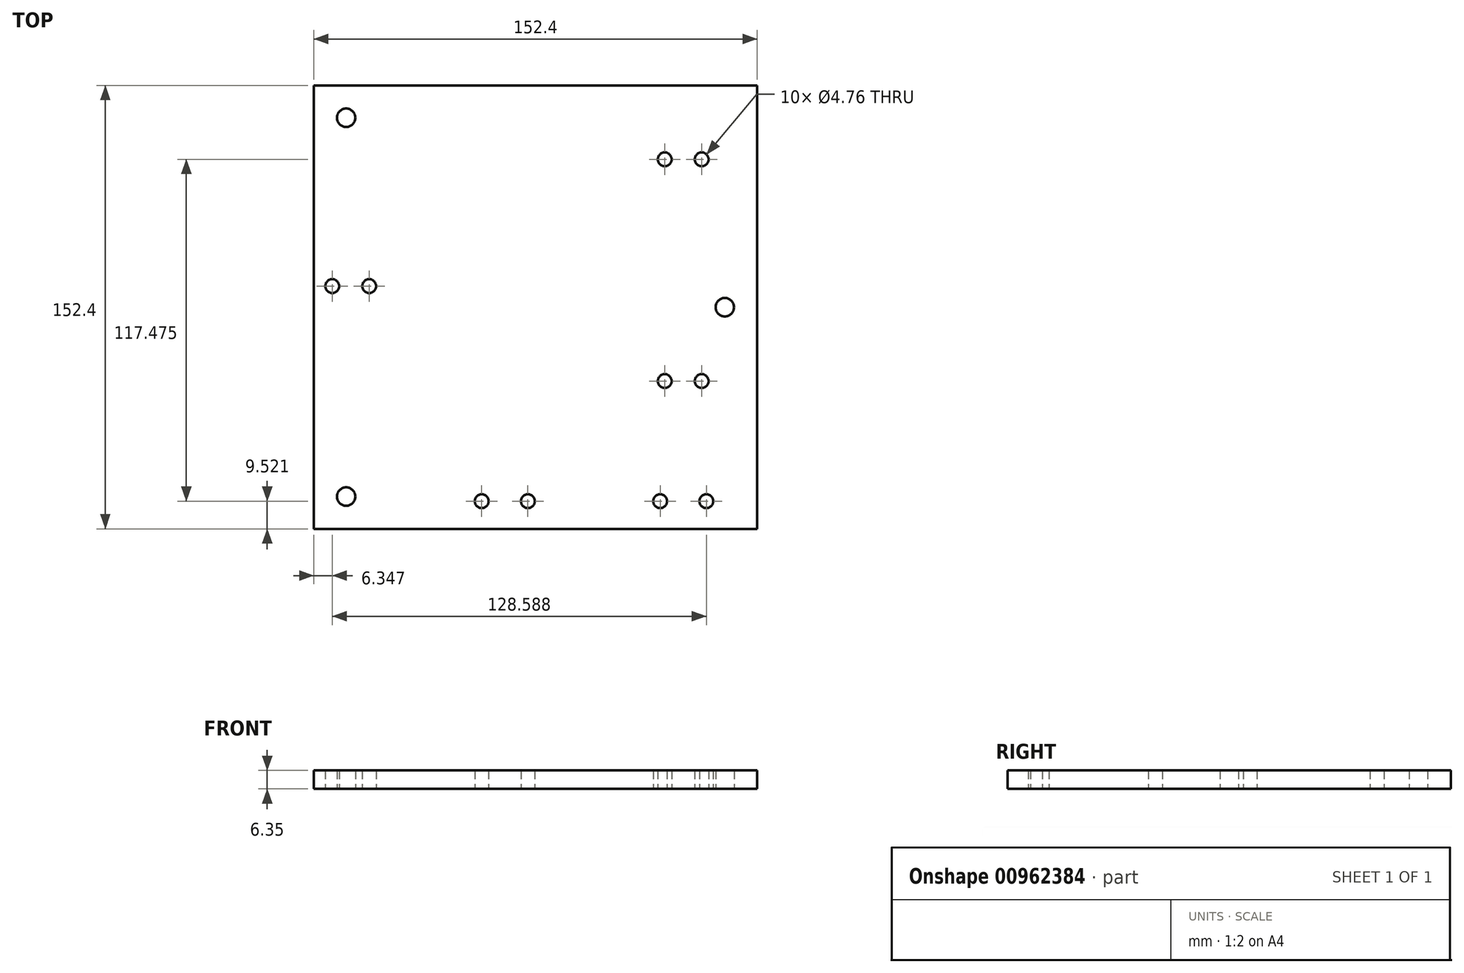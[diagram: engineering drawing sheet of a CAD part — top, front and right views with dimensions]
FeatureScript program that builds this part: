
annotation { "Feature Type Name" : "Feature", "Feature Type Description" : "" }
export const myFeature = defineFeature(function(context is Context, id is Id, definition is map)
    precondition{}
    {
        {
            var Q0;
            Q0=qCreatedBy(makeId("Top.planeOp"),FACE);
            var sketch = newSketch(context, id + "F0", { "sketchPlane" : qUnion([Q0])});
            skLineSegment(sketch, "E0.bottom", {"start": v(-78.32, 75.32) * mm, "end": v(74.08, 75.32) * mm});
            skLineSegment(sketch, "E0.top", {"start": v(-78.32, -77.08) * mm, "end": v(74.08, -77.08) * mm});
            skLineSegment(sketch, "E0.left", {"start": v(-78.32, 75.32) * mm, "end": v(-78.32, -77.08) * mm});
            skLineSegment(sketch, "E0.right", {"start": v(74.08, 75.32) * mm, "end": v(74.08, -77.08) * mm});
            skCircle(sketch, "E1", {"center": v(-67.21, -65.97) * mm, "radius": 3.18 * mm});
            skCircle(sketch, "E2", {"center": v(-67.21, 64.2) * mm, "radius": 3.18 * mm});
            skCircle(sketch, "E3", {"center": v(62.96, -0.88) * mm, "radius": 3.18 * mm});
            skCircle(sketch, "E4", {"center": v(42.33, -26.28) * mm, "radius": 6.35 * mm, "construction": true});
            skCircle(sketch, "E5", {"center": v(42.33, -26.28) * mm, "radius": 2.38 * mm});
            skCircle(sketch, "E6", {"center": v(42.33, 49.92) * mm, "radius": 6.35 * mm, "construction": true});
            skCircle(sketch, "E7", {"center": v(42.33, 49.92) * mm, "radius": 2.38 * mm});
            skCircle(sketch, "E8", {"center": v(-71.97, 6.35) * mm, "radius": 2.38 * mm});
            skCircle(sketch, "E9", {"center": v(-59.27, 6.35) * mm, "radius": 2.38 * mm});
            skLineSegment(sketch, "E10.bottom", {"start": v(-28.54, -77.08) * mm, "end": v(3.21, -77.08) * mm, "construction": true});
            skLineSegment(sketch, "E10.top", {"start": v(-28.54, -58.03) * mm, "end": v(3.21, -58.03) * mm, "construction": true});
            skLineSegment(sketch, "E10.left", {"start": v(-28.54, -77.08) * mm, "end": v(-28.54, -58.03) * mm, "construction": true});
            skLineSegment(sketch, "E10.right", {"start": v(3.21, -77.08) * mm, "end": v(3.21, -58.03) * mm, "construction": true});
            skCircle(sketch, "E11", {"center": v(-20.6, -67.56) * mm, "radius": 2.38 * mm});
            skCircle(sketch, "E12", {"center": v(-4.73, -67.56) * mm, "radius": 2.38 * mm});
            skLineSegment(sketch, "E13.bottom", {"start": v(32.8, -77.08) * mm, "end": v(64.55, -77.08) * mm, "construction": true});
            skLineSegment(sketch, "E13.top", {"start": v(32.8, -58.03) * mm, "end": v(64.55, -58.03) * mm, "construction": true});
            skLineSegment(sketch, "E13.left", {"start": v(32.8, -77.08) * mm, "end": v(32.8, -58.03) * mm, "construction": true});
            skLineSegment(sketch, "E13.right", {"start": v(64.55, -77.08) * mm, "end": v(64.55, -58.03) * mm, "construction": true});
            skCircle(sketch, "E14", {"center": v(40.74, -67.56) * mm, "radius": 2.38 * mm});
            skCircle(sketch, "E15", {"center": v(56.61, -67.56) * mm, "radius": 2.38 * mm});
            skLineSegment(sketch, "E16", {"start": v(48.68, 75.32) * mm, "end": v(48.68, -77.08) * mm});
            skCircle(sketch, "E17.MirrorC", {"center": v(55.03, 49.92) * mm, "radius": 2.38 * mm});
            skCircle(sketch, "E18.MirrorC", {"center": v(55.03, 49.92) * mm, "radius": 6.35 * mm, "construction": true});
            skCircle(sketch, "E19.MirrorC", {"center": v(55.03, -26.28) * mm, "radius": 2.38 * mm});
            skCircle(sketch, "E20.MirrorC", {"center": v(55.03, -26.28) * mm, "radius": 6.35 * mm, "construction": true});
            skSolve(sketch);
        }
        {
            var Q0;
            Q0 = qSketchRegion(id + "F0", true);
            extrude(context, id + "F1", {"entities" : qUnion([Q0]), "depth" : 6.35 * mm, "offsetDistance" : 25.4 * mm});
        }
    });
